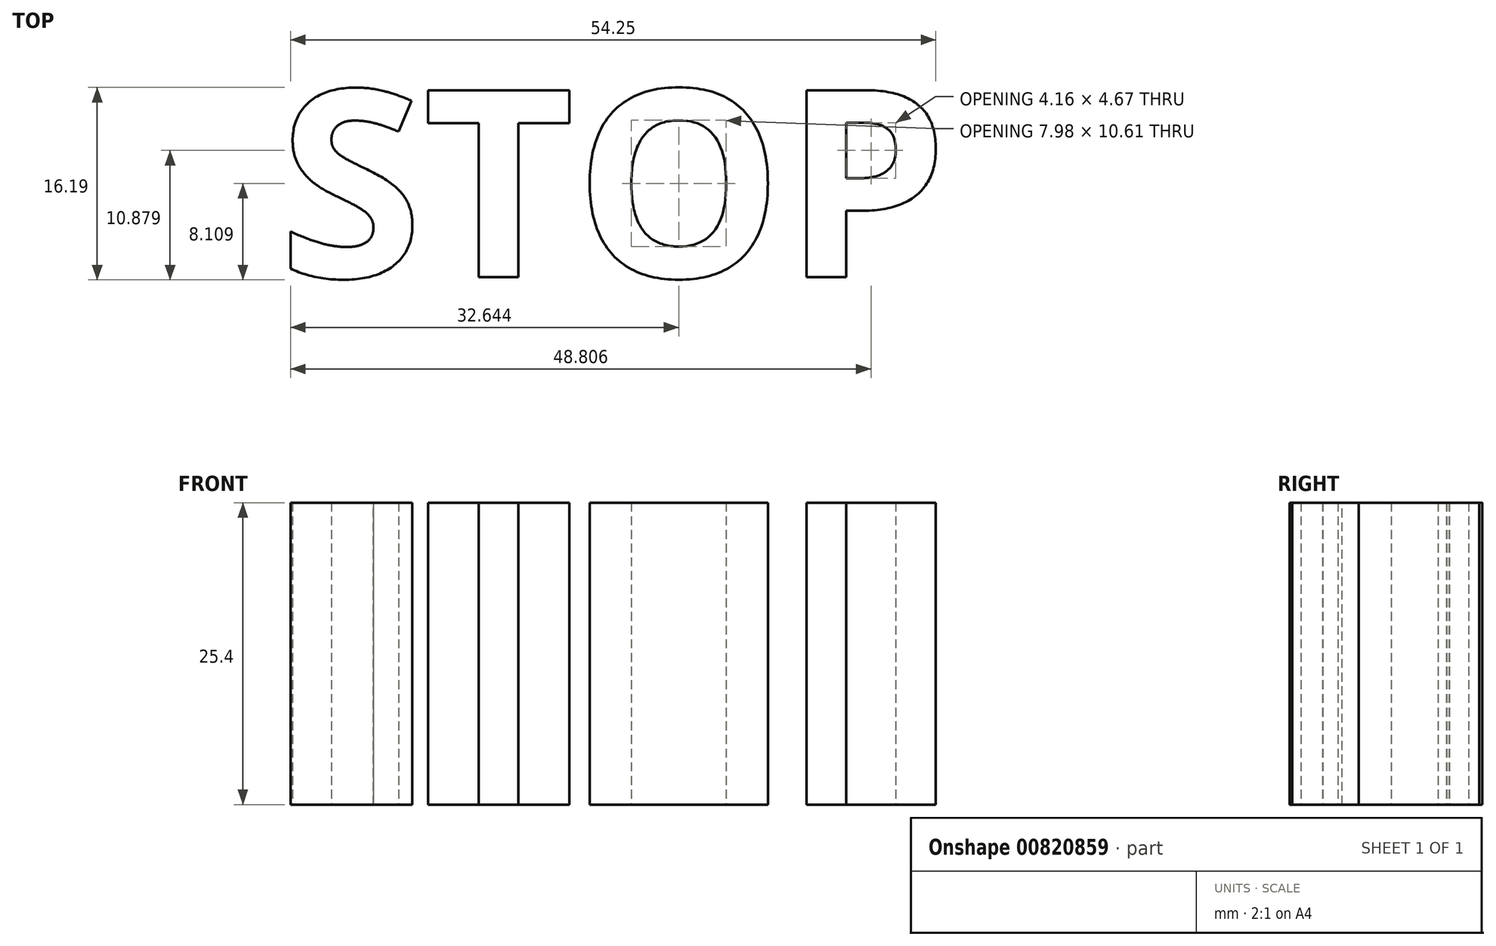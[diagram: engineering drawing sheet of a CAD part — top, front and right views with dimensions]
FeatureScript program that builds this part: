
annotation { "Feature Type Name" : "Feature", "Feature Type Description" : "" }
export const myFeature = defineFeature(function(context is Context, id is Id, definition is map)
    precondition{}
    {
        {
            var Q0;
            Q0=qCreatedBy(makeId("Top.planeOp"),FACE);
            var sketch = newSketch(context, id + "F0", { "sketchPlane" : qUnion([Q0])});
            skText(sketch, "E0", { "text": "STOP", "fontName": "OpenSans-Bold.ttf"});
            const initialGuessF0  = {"E0": [-0.0279, -0.00815, 1, 0, 0.01586]};
            skSetInitialGuess(sketch, initialGuessF0);
            skSolve(sketch);
        }
        {
            var Q0;
            Q0 = qSketchRegion(id + "F0", true);
            extrude(context, id + "F1", {"entities" : qUnion([Q0]), "depth" : 25.4 * mm, "offsetDistance" : 25.4 * mm, "symmetric" : true});
        }
    });
